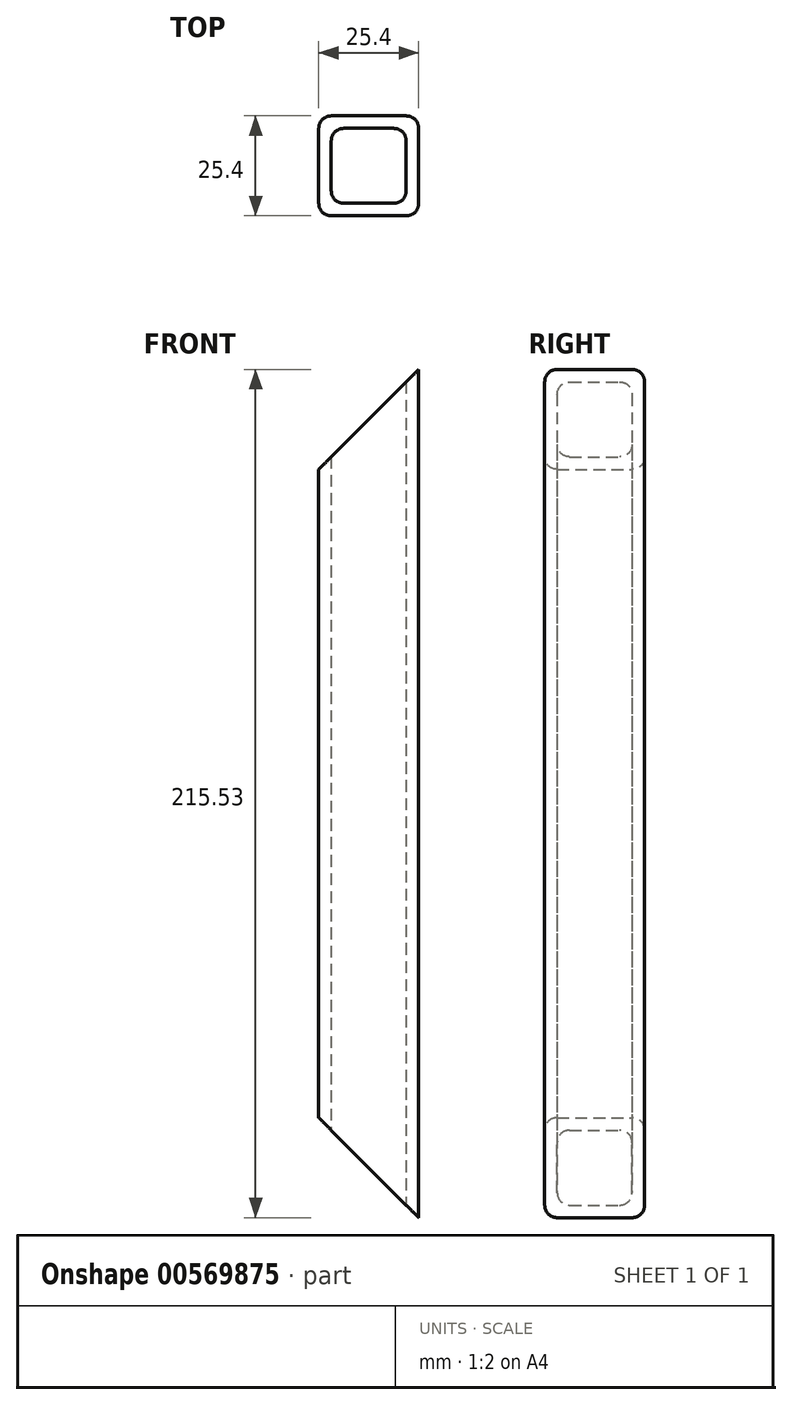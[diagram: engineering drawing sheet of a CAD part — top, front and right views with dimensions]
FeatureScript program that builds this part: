
annotation { "Feature Type Name" : "Feature", "Feature Type Description" : "" }
export const myFeature = defineFeature(function(context is Context, id is Id, definition is map)
    precondition{}
    {
        {
            var Q0;
            Q0=qCreatedBy(makeId("Top.planeOp"),FACE);
            var sketch = newSketch(context, id + "F0", { "sketchPlane" : qUnion([Q0])});
            skLineSegment(sketch, "E0.bottom", {"start": v(8.79, -11.72) * mm, "end": v(-10.26, -11.72) * mm});
            skLineSegment(sketch, "E0.top", {"start": v(8.79, 13.68) * mm, "end": v(-10.26, 13.68) * mm});
            skLineSegment(sketch, "E0.left", {"start": v(11.96, -8.55) * mm, "end": v(11.96, 10.5) * mm});
            skLineSegment(sketch, "E0.right", {"start": v(-13.44, -8.55) * mm, "end": v(-13.44, 10.5) * mm});
            skLineSegment(sketch, "E1.bottom", {"start": v(5.61, -8.55) * mm, "end": v(-7.09, -8.55) * mm});
            skLineSegment(sketch, "E1.top", {"start": v(5.61, 10.5) * mm, "end": v(-7.09, 10.5) * mm});
            skLineSegment(sketch, "E1.left", {"start": v(8.79, -5.37) * mm, "end": v(8.79, 7.33) * mm});
            skLineSegment(sketch, "E1.right", {"start": v(-10.26, -5.37) * mm, "end": v(-10.26, 7.33) * mm});
            skPoint(sketch, "E2.visualSharp", {"position": v(8.79, 10.5) * mm});
            skArc(sketch, "E2.filletArc", {"start": v(8.79, 7.33) * mm, "mid": v(7.86, 9.57) * mm, "end": v(5.61, 10.5) * mm});
            skPoint(sketch, "E3.visualSharp", {"position": v(-10.26, 10.5) * mm});
            skArc(sketch, "E3.filletArc", {"start": v(-7.09, 10.5) * mm, "mid": v(-9.34, 9.57) * mm, "end": v(-10.26, 7.33) * mm});
            skPoint(sketch, "E4.visualSharp", {"position": v(-10.26, -8.55) * mm});
            skArc(sketch, "E4.filletArc", {"start": v(-10.26, -5.37) * mm, "mid": v(-9.34, -7.62) * mm, "end": v(-7.09, -8.55) * mm});
            skPoint(sketch, "E5.visualSharp", {"position": v(8.79, -8.55) * mm});
            skArc(sketch, "E5.filletArc", {"start": v(5.61, -8.55) * mm, "mid": v(7.86, -7.62) * mm, "end": v(8.79, -5.37) * mm});
            skPoint(sketch, "E6.visualSharp", {"position": v(11.96, 13.68) * mm});
            skArc(sketch, "E6.filletArc", {"start": v(11.96, 10.5) * mm, "mid": v(11.03, 12.75) * mm, "end": v(8.79, 13.68) * mm});
            skPoint(sketch, "E7.visualSharp", {"position": v(-13.44, 13.68) * mm});
            skArc(sketch, "E7.filletArc", {"start": v(-10.26, 13.68) * mm, "mid": v(-12.51, 12.75) * mm, "end": v(-13.44, 10.5) * mm});
            skPoint(sketch, "E8.visualSharp", {"position": v(-13.44, -11.72) * mm});
            skArc(sketch, "E8.filletArc", {"start": v(-13.44, -8.55) * mm, "mid": v(-12.51, -10.8) * mm, "end": v(-10.26, -11.72) * mm});
            skPoint(sketch, "E9.visualSharp", {"position": v(11.96, -11.72) * mm});
            skArc(sketch, "E9.filletArc", {"start": v(8.79, -11.72) * mm, "mid": v(11.03, -10.8) * mm, "end": v(11.96, -8.55) * mm});
            skSolve(sketch);
        }
        {
            var Q0;
            Q0 = qSketchRegion(id + "F0", true);
            extrude(context, id + "F1", {"entities" : qUnion([Q0]), "depth" : 215.53 * mm, "offsetDistance" : 25.4 * mm});
        }
        {
            var Q0;
            Q0=qCreatedBy(makeId("Front.planeOp"),FACE);
            var sketch = newSketch(context, id + "F2", { "sketchPlane" : qUnion([Q0])});
            skLineSegment(sketch, "E10.bottom", {"start": v(11.96, 0) * mm, "end": v(-13.44, 0) * mm});
            skLineSegment(sketch, "E10.top", {"start": v(11.96, 25.4) * mm, "end": v(-13.44, 25.4) * mm});
            skLineSegment(sketch, "E10.left", {"start": v(11.96, 0) * mm, "end": v(11.96, 25.4) * mm});
            skLineSegment(sketch, "E10.right", {"start": v(-13.44, 0) * mm, "end": v(-13.44, 25.4) * mm});
            skLineSegment(sketch, "E11", {"start": v(-13.44, 25.4) * mm, "end": v(11.96, 0) * mm});
            skSolve(sketch);
        }
        {
            var Q0;
            Q0=qCreatedBy(makeId("Front.planeOp"),FACE);
            var sketch = newSketch(context, id + "F3", { "sketchPlane" : qUnion([Q0])});
            skLineSegment(sketch, "E12.bottom", {"start": v(11.96, 190.13) * mm, "end": v(-13.44, 190.13) * mm});
            skLineSegment(sketch, "E12.top", {"start": v(11.96, 215.53) * mm, "end": v(-13.44, 215.53) * mm});
            skLineSegment(sketch, "E12.left", {"start": v(11.96, 190.13) * mm, "end": v(11.96, 215.53) * mm});
            skLineSegment(sketch, "E12.right", {"start": v(-13.44, 190.13) * mm, "end": v(-13.44, 215.53) * mm});
            skLineSegment(sketch, "E13", {"start": v(-13.44, 190.13) * mm, "end": v(11.96, 215.53) * mm});
            skSolve(sketch);
        }
        {
            var Q0;
            Q0=makeQuery(id+"F2.imprint","IMPRINT",FACE,{"disambiguationData":[TD([[makeQuery(id+"F2.imprint","IMPRINT",EDGE,{"derivedFrom":sQuery(id+"F2.wireOp",EDGE,"E10.bottom")}),-1.0]])]});
            extrude(context, id + "F4", {"entities" : qUnion([Q0]), "operationType" : NewBodyOperationType.REMOVE, "depth" : 50.8 * mm, "offsetDistance" : 25.4 * mm, "symmetric" : true});
        }
        {
            var Q0;
            Q0=makeQuery(id+"F3.imprint","IMPRINT",FACE,{"disambiguationData":[TD([[makeQuery(id+"F3.imprint","IMPRINT",EDGE,{"derivedFrom":sQuery(id+"F3.wireOp",EDGE,"E12.top")}),1.0]])]});
            extrude(context, id + "F5", {"entities" : qUnion([Q0]), "operationType" : NewBodyOperationType.REMOVE, "depth" : 50.8 * mm, "offsetDistance" : 25.4 * mm, "symmetric" : true});
        }
    });
